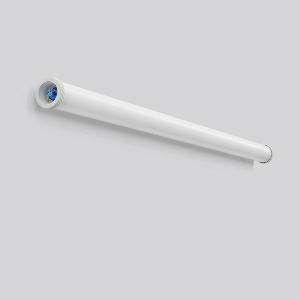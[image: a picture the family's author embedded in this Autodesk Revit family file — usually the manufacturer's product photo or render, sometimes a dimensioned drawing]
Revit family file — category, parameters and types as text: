
# Revit family: planox_tube_farm_601072_002_5_84f7
name_source: partatom
category: Lighting Fixtures
units: mm (PartAtom-declared; Revit-internal decimal feet)

## family parameters
Cut with Voids When Loaded = No
Host = Face
Light Source = No
Part Type = Normal
Room Calculation Point = No
Round Connector Dimension = Use Diameter
Shared = No

## types (1)
- PLANOX TUBE FARM (1 x LED Modul 840, 10000 lm, 4000)
    Apparent Load = 62 VA
    CIE Flux Codes = 44 74 91 92 100
    Color Rendering = 80
    Color Temperature = 4000
    Default Elevation = 1800 mm
    Description = Series: PLANOX TUBE FARM
Ammonia-resistant protective tube luminaire for tough requirements. Rack made of sheet steel, white powder coated. End caps made of plastic (polyamide) grey. Diffuser made of UV-resistant plastic (PMMA), opal. Symmetrical light distribution. Homogeneous light distribution. With accessories for wall, ceiling or pendant mounting. Driver integrated. Easy installation with the Plug+Play Wieland RST CLASSIC plug-in system. Mounting set must be ordered separately. Luminaire with limited surface temperature in accordance with EN 60598-2-24 for use in environments in which a deposit of conductive dust on the luminaire can be expected. Ammonia resistant : Suitable for the use in stables with livestock and agricultural side areas. Environmentally friendly and resource-saving due to replaceable components. 
Colour: white
Diameter: 78 mm
Length: 1564 mm
Lamp: LED
Socket: without socket
Colour temperature: 4000K
Colour rendering index (CRI): 83
System power: 62 W
Rated luminous flux: 10000 lm
Beam angle Down: 121° / 100°
Luminous efficiency: 161 lm/W
Control gear: Regulated power supply
Protection class: I
Type of protection: IP 67
    Height = 0 mm  [stored 0 ft]
    Lamp = 1 x LED Modul 840
    Lamp Light Flux = 10000 lm
    Lamp count = 1
    Length = 1564 mm
    Lifetime = 50000 h
    Luminous efficacy = 161 lm/W
    Manufacturer = RZB
    ModVariant = No
    Model = 601072.002.5
    Mounting Place = Ceiling
    Mounting Type = Surface mounted
    Number of Poles = 1
    OnlyDefault = Yes
    Power Factor = 1
    Product Name = PLANOX TUBE FARM
    Product group = Surface mounted luminaires for moist/humid enviroments
    ProductGroupID = 308
    Protection Class = Protection class I
    Protection Degree = Degree of protection
    RLX_Detail_Level = 1
    RLX_Emergency_Light_Flux = 0 lm
    RLX_Emergency_Type = 0
    RLX_Emergency_Type_DB = No
    RlxData = <blob elided: 34481 chars, md5=375eebea>
    Socket = socket
    Standby Power = 0 W
    System Light Flux = 10000 lm
    System Power = 62 W
    Type Comments = ALEA SPOT
    Type Image = 601072.002.5.jpg
    URL = http://relux.com
    VarID = ---
    Voltage = 0 V
    Weight = 0.00 kg
    Width = 0 mm  [stored 0 ft]

note: [stored X ft] marks values corroborated as IEEE doubles in the binary element streams (Revit-internal decimal feet)

## geometry (parser evidence)
native form markers: Blend x4, Sweep x12
no freeform markers — native parametric forms only
